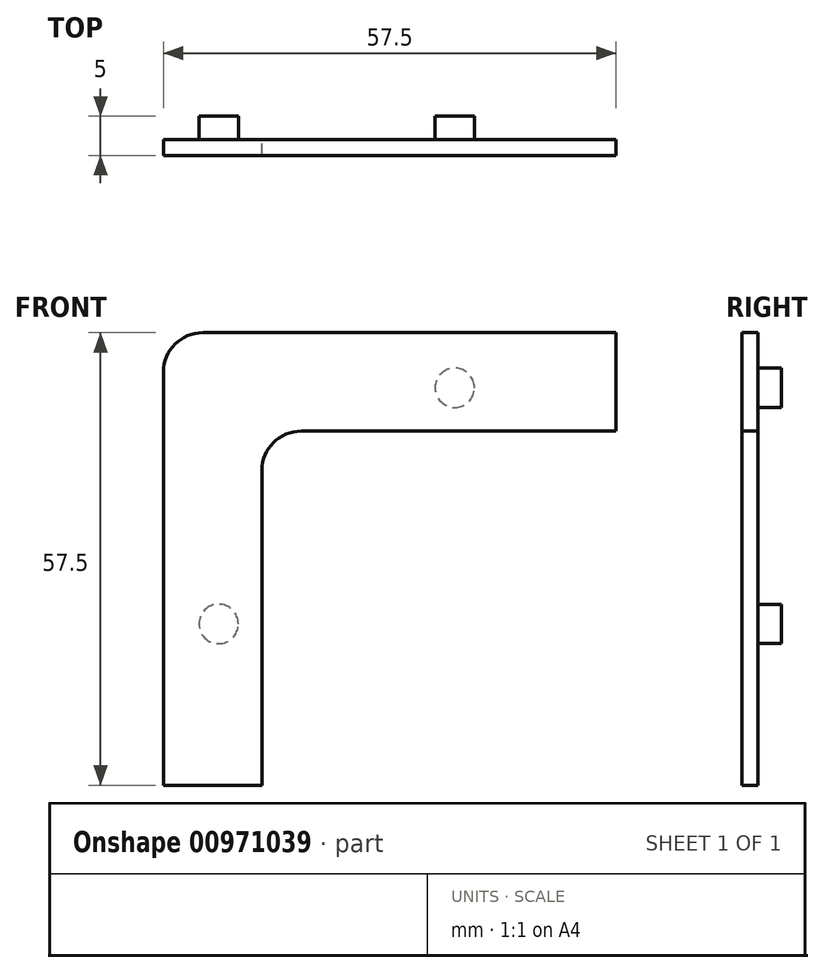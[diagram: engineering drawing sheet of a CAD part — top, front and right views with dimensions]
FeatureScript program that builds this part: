
annotation { "Feature Type Name" : "Feature", "Feature Type Description" : "" }
export const myFeature = defineFeature(function(context is Context, id is Id, definition is map)
    precondition{}
    {
        {
            var Q0;
            Q0=qCreatedBy(makeId("Front.planeOp"),FACE);
            var sketch = newSketch(context, id + "F0", { "sketchPlane" : qUnion([Q0])});
            skLineSegment(sketch, "E0", {"start": v(-12.5, 12.5) * mm, "end": v(-12.5, -45) * mm});
            skLineSegment(sketch, "E1", {"start": v(-12.5, -45) * mm, "end": v(0, -45) * mm});
            skLineSegment(sketch, "E2", {"start": v(0, -45) * mm, "end": v(0, 0) * mm});
            skLineSegment(sketch, "E3", {"start": v(0, 0) * mm, "end": v(45, 0) * mm});
            skLineSegment(sketch, "E4", {"start": v(45, 0) * mm, "end": v(45, 12.5) * mm});
            skLineSegment(sketch, "E5", {"start": v(45, 12.5) * mm, "end": v(-12.5, 12.5) * mm});
            skSolve(sketch);
        }
        {
            var Q0;
            Q0=makeQuery(id+"F0.imprint","IMPRINT",FACE,{"disambiguationData":[TD([[makeQuery(id+"F0.imprint","IMPRINT",EDGE,{"derivedFrom":sQuery(id+"F0.wireOp",EDGE,"E0")}),1.0]])]});
            extrude(context, id + "F1", {"entities" : qUnion([Q0]), "depth" : 2 * mm, "offsetDistance" : 25 * mm});
        }
        {
            var Q0;
            Q0=makeQuery(id+"F1.opExtrude","SWEPT_EDGE",EDGE,{"disambiguationData":[OSD([sQuery(id+"F0.wireOp",EDGE,"E0"),sQuery(id+"F0.wireOp",EDGE,"E5")])]});
            var Q1;
            Q1=makeQuery(id+"F1.opExtrude","SWEPT_EDGE",EDGE,{"disambiguationData":[OSD([sQuery(id+"F0.wireOp",EDGE,"E2"),sQuery(id+"F0.wireOp",EDGE,"E3")])]});
            fillet(context, id + "F2", {"entities" : qUnion([Q0, Q1]), "radius" : 5 * mm, "tangentPropagation" : true, "allowEdgeOverflow" : false});
        }
        {
            var Q0;
            Q0=qCreatedBy(makeId("Front.planeOp"),FACE);
            var sketch = newSketch(context, id + "F3", { "sketchPlane" : qUnion([Q0])});
            skCircle(sketch, "E6", {"center": v(-5.5, -24.5) * mm, "radius": 2.5 * mm});
            skCircle(sketch, "E7", {"center": v(24.5, 5.5) * mm, "radius": 2.5 * mm});
            skLineSegment(sketch, "E8", {"start": v(45, 5.5) * mm, "end": v(24.5, 5.5) * mm, "construction": true});
            skLineSegment(sketch, "E9", {"start": v(-5.5, -24.5) * mm, "end": v(-5.5, -45) * mm, "construction": true});
            skSolve(sketch);
        }
        {
            var Q0;
            Q0=makeQuery(id+"F3.imprint","IMPRINT",FACE,{"disambiguationData":[TD([[makeQuery(id+"F3.imprint","IMPRINT",EDGE,{"derivedFrom":sQuery(id+"F3.wireOp",EDGE,"E7")}),1.0]])]});
            var Q1;
            Q1=makeQuery(id+"F3.imprint","IMPRINT",FACE,{"disambiguationData":[TD([[makeQuery(id+"F3.imprint","IMPRINT",EDGE,{"derivedFrom":sQuery(id+"F3.wireOp",EDGE,"E6")}),1.0]])]});
            extrude(context, id + "F4", {"entities" : qUnion([Q0, Q1]), "operationType" : NewBodyOperationType.ADD, "oppositeDirection" : true, "depth" : 3 * mm, "offsetDistance" : 25 * mm});
        }
    });
